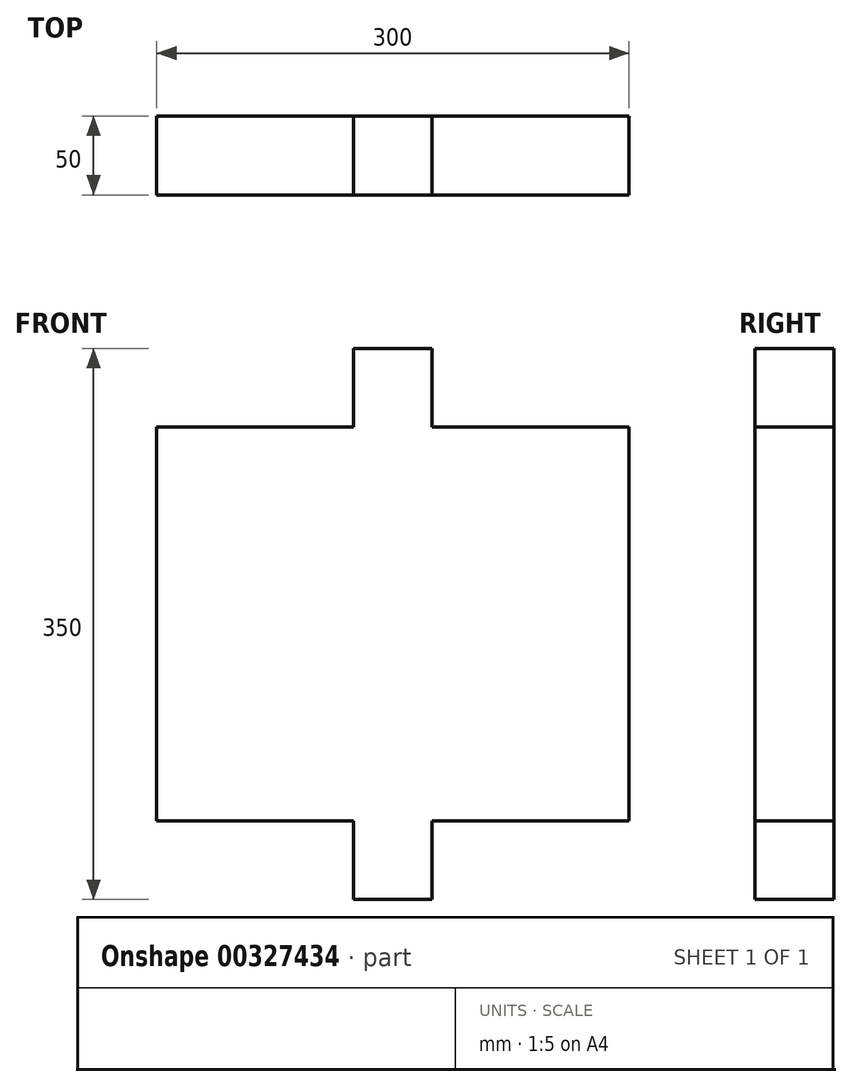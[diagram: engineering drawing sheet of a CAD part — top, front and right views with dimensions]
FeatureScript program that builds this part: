
annotation { "Feature Type Name" : "Feature", "Feature Type Description" : "" }
export const myFeature = defineFeature(function(context is Context, id is Id, definition is map)
    precondition{}
    {
        {
            var Q0;
            Q0=qCreatedBy(makeId("Front.planeOp"),FACE);
            var sketch = newSketch(context, id + "F0", { "sketchPlane" : qUnion([Q0])});
            skLineSegment(sketch, "E0.left", {"start": v(-181.3, 185.09) * mm, "end": v(-181.3, -64.91) * mm});
            skLineSegment(sketch, "E1", {"start": v(-181.3, -64.91) * mm, "end": v(-56.3, -64.91) * mm});
            skLineSegment(sketch, "E2", {"start": v(118.7, -64.91) * mm, "end": v(118.7, 185.09) * mm});
            skLineSegment(sketch, "E3", {"start": v(-56.3, 235.09) * mm, "end": v(-56.3, 185.09) * mm});
            skLineSegment(sketch, "E4", {"start": v(-6.3, 185.09) * mm, "end": v(-6.3, 235.09) * mm});
            skLineSegment(sketch, "E5", {"start": v(-56.3, 235.09) * mm, "end": v(-6.3, 235.09) * mm});
            skLineSegment(sketch, "E6", {"start": v(-56.3, 185.09) * mm, "end": v(-181.3, 185.09) * mm});
            skLineSegment(sketch, "E7", {"start": v(-6.3, 185.09) * mm, "end": v(118.7, 185.09) * mm});
            skLineSegment(sketch, "E8", {"start": v(-56.3, -64.91) * mm, "end": v(-56.3, -114.91) * mm});
            skLineSegment(sketch, "E9", {"start": v(-56.3, -114.91) * mm, "end": v(-6.3, -114.91) * mm});
            skLineSegment(sketch, "E10", {"start": v(-6.3, -114.91) * mm, "end": v(-6.3, -64.91) * mm});
            skLineSegment(sketch, "E11.trimOffspring", {"start": v(-6.3, -64.91) * mm, "end": v(118.7, -64.91) * mm});
            skSolve(sketch);
        }
        {
            var Q0;
            Q0 = qSketchRegion(id + "F0", true);
            extrude(context, id + "F1", {"entities" : qUnion([Q0]), "depth" : 50 * mm});
        }
    });
